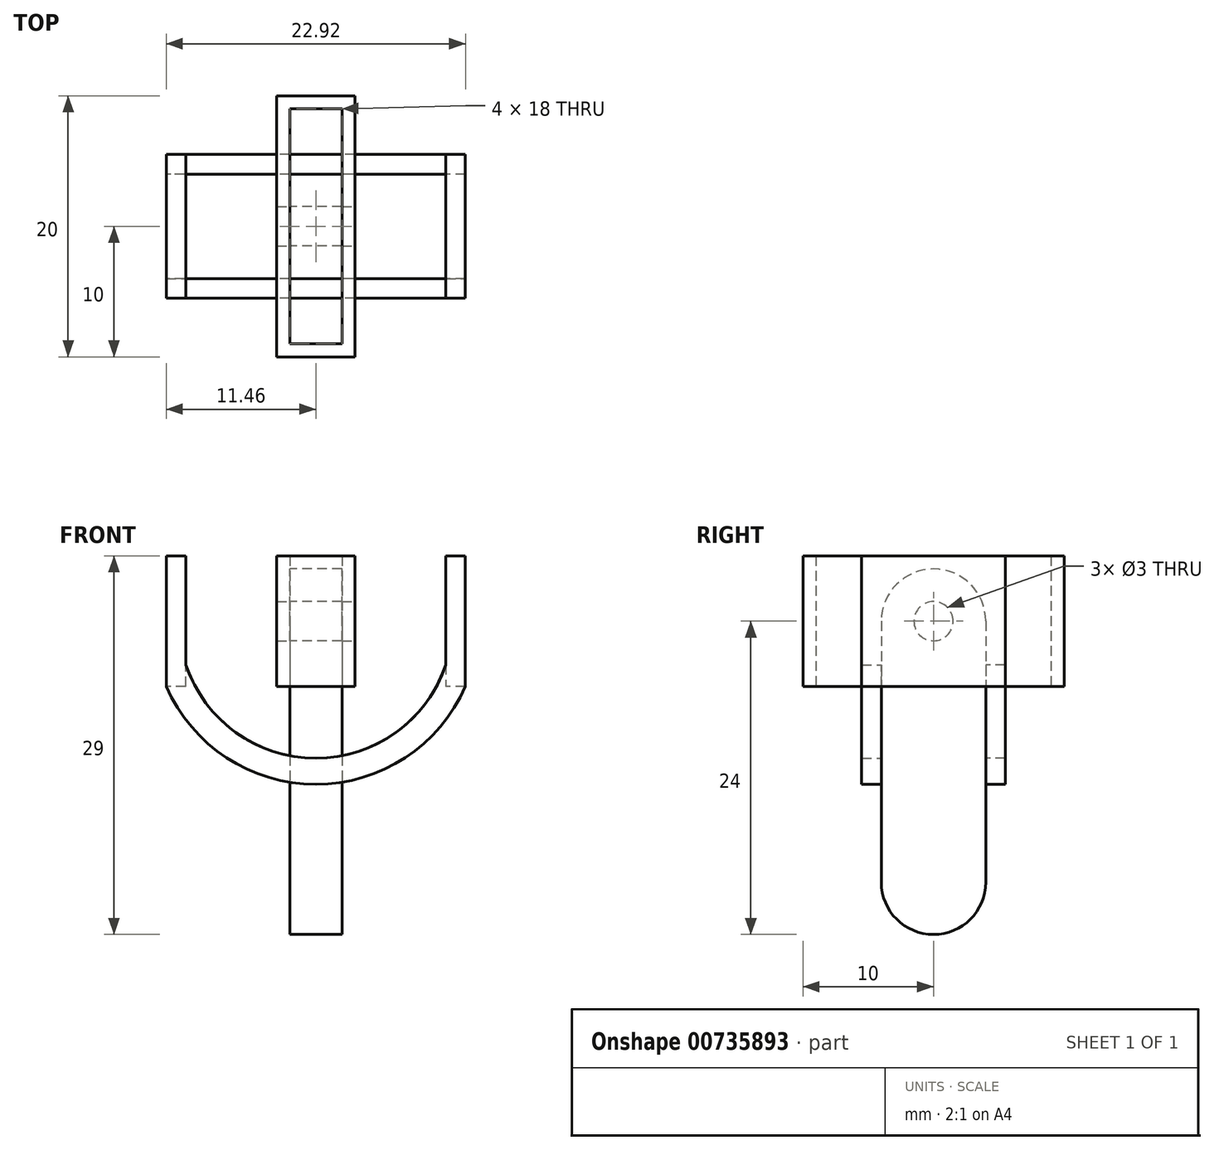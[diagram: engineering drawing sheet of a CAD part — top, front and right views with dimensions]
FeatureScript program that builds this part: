
annotation { "Feature Type Name" : "Feature", "Feature Type Description" : "" }
export const myFeature = defineFeature(function(context is Context, id is Id, definition is map)
    precondition{}
    {
        {
            var Q0;
            Q0=qCreatedBy(makeId("Right.planeOp"),FACE);
            var sketch = newSketch(context, id + "F0", { "sketchPlane" : qUnion([Q0])});
            skCircle(sketch, "E0", {"center": v(0, 0) * mm, "radius": 1.5 * mm});
            skCircle(sketch, "E1", {"center": v(0, 0) * mm, "radius": 4 * mm});
            skCircle(sketch, "E2", {"center": v(0, -20) * mm, "radius": 4 * mm});
            skLineSegment(sketch, "E3", {"start": v(-4, 0) * mm, "end": v(-4, -20) * mm});
            skLineSegment(sketch, "E4", {"start": v(4, 0) * mm, "end": v(4, -20) * mm});
            skSolve(sketch);
        }
        {
            var Q0;
            Q0=makeQuery(id+"F0.imprint","IMPRINT",FACE,{"disambiguationData":[TD([[makeQuery(id+"F0.imprint","IMPRINT",EDGE,{"derivedFrom":sQuery(id+"F0.wireOp",EDGE,"E0")}),-1.0]])]});
            var Q1;
            {var subQ0=sQuery(id+"F0.wireOp",EDGE,"E3");Q1=makeQuery(id+"F0.imprint","IMPRINT",FACE,{"disambiguationData":[TD([[makeQuery(id+"F0.imprint","IMPRINT",EDGE,{"derivedFrom":subQ0}),1.0]])]});}
            var Q2;
            {var subQ0=sQuery(id+"F0.wireOp",EDGE,"E2");var subQ1=makeQuery(id+"F0.imprint","INTERSECT",VERTEX,{"derivedFrom":[subQ0,sQuery(id+"F0.wireOp",EDGE,"E3")]});Q2=makeQuery(id+"F0.imprint","IMPRINT",FACE,{"disambiguationData":[TD([[makeQuery(id+"F0.imprint","IMPRINT",EDGE,{"disambiguationData":[TD([[subQ1,1.0]])],"derivedFrom":subQ0}),1.0]])]});}
            extrude(context, id + "F1", {"entities" : qUnion([Q0, Q1, Q2]), "endBound" : BoundingType.SYMMETRIC, "depth" : 4 * mm, "offsetDistance" : 25 * mm});
        }
        {
            var Q0;
            Q0=qCreatedBy(makeId("Top.planeOp"),FACE);
            var sketch = newSketch(context, id + "F2", { "sketchPlane" : qUnion([Q0])});
            skLineSegment(sketch, "E5.bottom", {"start": v(-2, 9) * mm, "end": v(2, 9) * mm});
            skLineSegment(sketch, "E5.top", {"start": v(-2, -9) * mm, "end": v(2, -9) * mm});
            skLineSegment(sketch, "E5.left", {"start": v(-2, 9) * mm, "end": v(-2, -9) * mm});
            skLineSegment(sketch, "E5.right", {"start": v(2, 9) * mm, "end": v(2, -9) * mm});
            skLineSegment(sketch, "E6.bottom", {"start": v(-3, 10) * mm, "end": v(3, 10) * mm});
            skLineSegment(sketch, "E6.top", {"start": v(-3, -10) * mm, "end": v(3, -10) * mm});
            skLineSegment(sketch, "E6.left", {"start": v(-3, 10) * mm, "end": v(-3, -10) * mm});
            skLineSegment(sketch, "E6.right", {"start": v(3, 10) * mm, "end": v(3, -10) * mm});
            skSolve(sketch);
        }
        {
            var Q0;
            Q0=makeQuery(id+"F2.imprint","IMPRINT",FACE,{"disambiguationData":[TD([[makeQuery(id+"F2.imprint","IMPRINT",EDGE,{"derivedFrom":sQuery(id+"F2.wireOp",EDGE,"E5.bottom")}),1.0]])]});
            extrude(context, id + "F3", {"entities" : qUnion([Q0]), "endBound" : BoundingType.SYMMETRIC, "depth" : 10 * mm, "offsetDistance" : 25 * mm});
        }
        {
            var Q0;
            Q0=makeQuery(id+"F0.imprint","IMPRINT",FACE,{"disambiguationData":[TD([[makeQuery(id+"F0.imprint","IMPRINT",EDGE,{"derivedFrom":sQuery(id+"F0.wireOp",EDGE,"E0")}),1.0]])]});
            extrude(context, id + "F4", {"entities" : qUnion([Q0]), "operationType" : NewBodyOperationType.REMOVE, "endBound" : BoundingType.SYMMETRIC, "oppositeDirection" : true, "depth" : 25 * mm, "offsetDistance" : 25 * mm});
        }
        {
            var Q0;
            Q0=makeQuery(id+"F1.opExtrude","SWEPT_FACE",FACE,{"disambiguationData":[OSD([sQuery(id+"F0.wireOp",EDGE,"E4")])]});
            var sketch = newSketch(context, id + "F5", { "sketchPlane" : qUnion([Q0])});
            skCircle(sketch, "E7", {"center": v(0, 0) * mm, "radius": 10.5 * mm});
            skCircle(sketch, "E8", {"center": v(0, 0) * mm, "radius": 12.5 * mm});
            skLineSegment(sketch, "E9", {"start": v(-11.46, 5) * mm, "end": v(11.46, 5) * mm});
            skLineSegment(sketch, "E10", {"start": v(-11.46, -5) * mm, "end": v(11.46, -5) * mm});
            skLineSegment(sketch, "E11", {"start": v(-11.46, 5) * mm, "end": v(-11.46, -5) * mm});
            skLineSegment(sketch, "E12", {"start": v(11.46, 5) * mm, "end": v(11.46, -5) * mm});
            skLineSegment(sketch, "E13", {"start": v(9.96, 5) * mm, "end": v(9.96, -5) * mm});
            skLineSegment(sketch, "E14", {"start": v(-9.96, 5) * mm, "end": v(-9.96, -5) * mm});
            skSolve(sketch);
        }
        {
            var Q0;
            {var subQ6=sQuery(id+"F5.wireOp",EDGE,"E11");Q0=makeQuery(id+"F5.imprint","IMPRINT",FACE,{"disambiguationData":[TD([[makeQuery(id+"F5.imprint","IMPRINT",EDGE,{"derivedFrom":subQ6}),1.0]])]});}
            var Q1;
            {var subQ0=sQuery(id+"F5.wireOp",EDGE,"lFEVrdAN-HZwF-8sQD-rMAo-F9QIEANWM2wr");Q1=makeQuery(id+"F5.imprint","IMPRINT",FACE,{"disambiguationData":[TD([[makeQuery(id+"F5.imprint","IMPRINT",EDGE,{"derivedFrom":subQ0}),-1.0]])]});}
            var Q2;
            {var subQ3=sQuery(id+"F5.wireOp",EDGE,"E7");var subQ7=makeQuery(id+"F5.imprint","INTERSECT",VERTEX,{"disambiguationData":[OD(0.0)],"derivedFrom":[subQ3,sQuery(id+"F5.wireOp",EDGE,"iSYoZpPV-LOci-Hl4O-fSi4-jdDNIl23jevi")]});Q2=makeQuery(id+"F5.imprint","IMPRINT",FACE,{"disambiguationData":[TD([[makeQuery(id+"F5.imprint","IMPRINT",EDGE,{"disambiguationData":[TD([[subQ7,-1.0]])],"derivedFrom":subQ3}),-1.0]])]});}
            var Q3;
            {var subQ0=sQuery(id+"F5.wireOp",EDGE,"E7");var subQ1=sQuery(id+"F0.wireOp",EDGE,"E4");var subQ2=makeQuery(id+"F1.opExtrude","CAP_EDGE",EDGE,{"disambiguationData":[OSD([subQ1])],"isStart":false});var subQ3=makeQuery(id+"F5.imprint","INTERSECT",VERTEX,{"derivedFrom":[subQ2,subQ0]});Q3=makeQuery(id+"F5.imprint","IMPRINT",FACE,{"disambiguationData":[TD([[makeQuery(id+"F5.imprint","IMPRINT",EDGE,{"disambiguationData":[TD([[subQ3,-1.0]])],"derivedFrom":subQ0}),-1.0]])]});}
            var Q4;
            {var subQ3=sQuery(id+"F5.wireOp",EDGE,"E7");var subQ7=makeQuery(id+"F5.imprint","INTERSECT",VERTEX,{"disambiguationData":[OD(1.0)],"derivedFrom":[subQ3,sQuery(id+"F5.wireOp",EDGE,"iSYoZpPV-LOci-Hl4O-fSi4-jdDNIl23jevi")]});Q4=makeQuery(id+"F5.imprint","IMPRINT",FACE,{"disambiguationData":[TD([[makeQuery(id+"F5.imprint","IMPRINT",EDGE,{"disambiguationData":[TD([[subQ7,1.0]])],"derivedFrom":subQ3}),-1.0]])]});}
            var Q5;
            {var subQ6=sQuery(id+"F5.wireOp",EDGE,"E12");Q5=makeQuery(id+"F5.imprint","IMPRINT",FACE,{"disambiguationData":[TD([[makeQuery(id+"F5.imprint","IMPRINT",EDGE,{"derivedFrom":subQ6}),-1.0]])]});}
            var Q6;
            {var subQ0=sQuery(id+"F5.wireOp",EDGE,"WG5NRfXU-aEiA-IK5w-2DdL-H3FO2lLHFPoR");Q6=makeQuery(id+"F5.imprint","IMPRINT",FACE,{"disambiguationData":[TD([[makeQuery(id+"F5.imprint","IMPRINT",EDGE,{"derivedFrom":subQ0}),1.0]])]});}
            var Q7;
            {var subQ0=sQuery(id+"F5.wireOp",EDGE,"E13");var subQ1=sQuery(id+"F5.wireOp",EDGE,"E7");var subQ2=makeQuery(id+"F5.imprint","INTERSECT",VERTEX,{"disambiguationData":[OD(0.0)],"derivedFrom":[subQ1,subQ0]});Q7=makeQuery(id+"F5.imprint","IMPRINT",FACE,{"disambiguationData":[TD([[makeQuery(id+"F5.imprint","IMPRINT",EDGE,{"disambiguationData":[TD([[subQ2,1.0]])],"derivedFrom":subQ1}),1.0]])]});}
            var Q8;
            {var subQ0=sQuery(id+"F5.wireOp",EDGE,"E10");var subQ2=sQuery(id+"F5.wireOp",EDGE,"E7");var subQ3=makeQuery(id+"F5.imprint","INTERSECT",VERTEX,{"disambiguationData":[OD(1.0)],"derivedFrom":[subQ2,subQ0]});Q8=makeQuery(id+"F5.imprint","IMPRINT",FACE,{"disambiguationData":[TD([[makeQuery(id+"F5.imprint","IMPRINT",EDGE,{"disambiguationData":[TD([[subQ3,1.0]])],"derivedFrom":subQ2}),-1.0]])]});}
            var Q9;
            {var subQ0=sQuery(id+"F5.wireOp",EDGE,"E10");var subQ4=sQuery(id+"F5.wireOp",EDGE,"E7");var subQ5=makeQuery(id+"F5.imprint","INTERSECT",VERTEX,{"disambiguationData":[OD(0.0)],"derivedFrom":[subQ4,subQ0]});Q9=makeQuery(id+"F5.imprint","IMPRINT",FACE,{"disambiguationData":[TD([[makeQuery(id+"F5.imprint","IMPRINT",EDGE,{"disambiguationData":[TD([[subQ5,-1.0]])],"derivedFrom":subQ4}),-1.0]])]});}
            var Q10;
            {var subQ0=sQuery(id+"F5.wireOp",EDGE,"E14");var subQ1=sQuery(id+"F5.wireOp",EDGE,"E7");var subQ2=makeQuery(id+"F5.imprint","INTERSECT",VERTEX,{"disambiguationData":[OD(1.0)],"derivedFrom":[subQ1,subQ0]});Q10=makeQuery(id+"F5.imprint","IMPRINT",FACE,{"disambiguationData":[TD([[makeQuery(id+"F5.imprint","IMPRINT",EDGE,{"disambiguationData":[TD([[subQ2,-1.0]])],"derivedFrom":subQ1}),-1.0]])]});}
            var Q11;
            {var subQ0=sQuery(id+"F5.wireOp",EDGE,"E14");var subQ1=sQuery(id+"F5.wireOp",EDGE,"E7");var subQ2=makeQuery(id+"F5.imprint","INTERSECT",VERTEX,{"disambiguationData":[OD(0.0)],"derivedFrom":[subQ1,subQ0]});Q11=makeQuery(id+"F5.imprint","IMPRINT",FACE,{"disambiguationData":[TD([[makeQuery(id+"F5.imprint","IMPRINT",EDGE,{"disambiguationData":[TD([[subQ2,-1.0]])],"derivedFrom":subQ1}),1.0]])]});}
            var Q12;
            {var subQ0=sQuery(id+"F5.wireOp",EDGE,"E10");var subQ1=sQuery(id+"F5.wireOp",EDGE,"E7");var subQ2=makeQuery(id+"F5.imprint","INTERSECT",VERTEX,{"disambiguationData":[OD(1.0)],"derivedFrom":[subQ1,subQ0]});Q12=makeQuery(id+"F5.imprint","IMPRINT",FACE,{"disambiguationData":[TD([[makeQuery(id+"F5.imprint","IMPRINT",EDGE,{"disambiguationData":[TD([[subQ2,-1.0]])],"derivedFrom":subQ1}),-1.0]])]});}
            extrude(context, id + "F6", {"entities" : qUnion([Q0, Q1, Q2, Q3, Q4, Q5, Q6, Q7, Q8, Q9, Q10, Q11, Q12]), "depth" : 1.5 * mm, "offsetDistance" : 25 * mm});
        }
        {
            var Q0;
            {var subQ6=sQuery(id+"F5.wireOp",EDGE,"E12");Q0=makeQuery(id+"F5.imprint","IMPRINT",FACE,{"disambiguationData":[TD([[makeQuery(id+"F5.imprint","IMPRINT",EDGE,{"derivedFrom":subQ6}),-1.0]])]});}
            var Q1;
            {var subQ0=sQuery(id+"F5.wireOp",EDGE,"WG5NRfXU-aEiA-IK5w-2DdL-H3FO2lLHFPoR");Q1=makeQuery(id+"F5.imprint","IMPRINT",FACE,{"disambiguationData":[TD([[makeQuery(id+"F5.imprint","IMPRINT",EDGE,{"derivedFrom":subQ0}),1.0]])]});}
            var Q2;
            {var subQ0=sQuery(id+"F5.wireOp",EDGE,"lFEVrdAN-HZwF-8sQD-rMAo-F9QIEANWM2wr");Q2=makeQuery(id+"F5.imprint","IMPRINT",FACE,{"disambiguationData":[TD([[makeQuery(id+"F5.imprint","IMPRINT",EDGE,{"derivedFrom":subQ0}),-1.0]])]});}
            var Q3;
            {var subQ6=sQuery(id+"F5.wireOp",EDGE,"E11");Q3=makeQuery(id+"F5.imprint","IMPRINT",FACE,{"disambiguationData":[TD([[makeQuery(id+"F5.imprint","IMPRINT",EDGE,{"derivedFrom":subQ6}),1.0]])]});}
            var Q4;
            {var subQ0=sQuery(id+"F5.wireOp",EDGE,"E13");var subQ1=sQuery(id+"F5.wireOp",EDGE,"E7");var subQ2=makeQuery(id+"F5.imprint","INTERSECT",VERTEX,{"disambiguationData":[OD(0.0)],"derivedFrom":[subQ1,subQ0]});Q4=makeQuery(id+"F5.imprint","IMPRINT",FACE,{"disambiguationData":[TD([[makeQuery(id+"F5.imprint","IMPRINT",EDGE,{"disambiguationData":[TD([[subQ2,1.0]])],"derivedFrom":subQ1}),1.0]])]});}
            var Q5;
            {var subQ0=sQuery(id+"F5.wireOp",EDGE,"E14");var subQ1=sQuery(id+"F5.wireOp",EDGE,"E7");var subQ2=makeQuery(id+"F5.imprint","INTERSECT",VERTEX,{"disambiguationData":[OD(0.0)],"derivedFrom":[subQ1,subQ0]});Q5=makeQuery(id+"F5.imprint","IMPRINT",FACE,{"disambiguationData":[TD([[makeQuery(id+"F5.imprint","IMPRINT",EDGE,{"disambiguationData":[TD([[subQ2,-1.0]])],"derivedFrom":subQ1}),1.0]])]});}
            var Q6;
            Q6=makeQuery(id+"F1.opExtrude","SWEPT_FACE",FACE,{"disambiguationData":[OSD([sQuery(id+"F0.wireOp",EDGE,"E3")])]});
            extrude(context, id + "F7", {"entities" : qUnion([Q0, Q1, Q2, Q3, Q4, Q5]), "operationType" : NewBodyOperationType.ADD, "endBound" : BoundingType.UP_TO_SURFACE, "oppositeDirection" : true, "depth" : 25 * mm, "endBoundEntityFace" : qUnion([Q6]), "offsetDistance" : 25 * mm});
        }
        {
            var Q0;
            {var subQ6=sQuery(id+"F5.wireOp",EDGE,"E11");Q0=makeQuery(id+"F5.imprint","IMPRINT",FACE,{"disambiguationData":[TD([[makeQuery(id+"F5.imprint","IMPRINT",EDGE,{"derivedFrom":subQ6}),1.0]])]});}
            var Q1;
            {var subQ0=sQuery(id+"F5.wireOp",EDGE,"lFEVrdAN-HZwF-8sQD-rMAo-F9QIEANWM2wr");Q1=makeQuery(id+"F5.imprint","IMPRINT",FACE,{"disambiguationData":[TD([[makeQuery(id+"F5.imprint","IMPRINT",EDGE,{"derivedFrom":subQ0}),-1.0]])]});}
            var Q2;
            {var subQ0=sQuery(id+"F5.wireOp",EDGE,"WG5NRfXU-aEiA-IK5w-2DdL-H3FO2lLHFPoR");Q2=makeQuery(id+"F5.imprint","IMPRINT",FACE,{"disambiguationData":[TD([[makeQuery(id+"F5.imprint","IMPRINT",EDGE,{"derivedFrom":subQ0}),1.0]])]});}
            var Q3;
            {var subQ6=sQuery(id+"F5.wireOp",EDGE,"E12");Q3=makeQuery(id+"F5.imprint","IMPRINT",FACE,{"disambiguationData":[TD([[makeQuery(id+"F5.imprint","IMPRINT",EDGE,{"derivedFrom":subQ6}),-1.0]])]});}
            var Q4;
            {var subQ3=makeQuery(id+"F1.opExtrude","CAP_EDGE",EDGE,{"disambiguationData":[OSD([sQuery(id+"F0.wireOp",EDGE,"E4")])],"isStart":true});var subQ5=sQuery(id+"F5.wireOp",EDGE,"E8");var subQ7=makeQuery(id+"F5.imprint","INTERSECT",VERTEX,{"derivedFrom":[subQ3,subQ5]});Q4=makeQuery(id+"F5.imprint","IMPRINT",FACE,{"disambiguationData":[TD([[makeQuery(id+"F5.imprint","IMPRINT",EDGE,{"disambiguationData":[TD([[subQ7,1.0]])],"derivedFrom":subQ3}),1.0]])]});}
            var Q5;
            {var subQ3=makeQuery(id+"F1.opExtrude","CAP_EDGE",EDGE,{"disambiguationData":[OSD([sQuery(id+"F0.wireOp",EDGE,"E4")])],"isStart":false});var subQ5=sQuery(id+"F5.wireOp",EDGE,"E8");var subQ6=makeQuery(id+"F5.imprint","INTERSECT",VERTEX,{"derivedFrom":[subQ3,subQ5]});Q5=makeQuery(id+"F5.imprint","IMPRINT",FACE,{"disambiguationData":[TD([[makeQuery(id+"F5.imprint","IMPRINT",EDGE,{"disambiguationData":[TD([[subQ6,1.0]])],"derivedFrom":subQ3}),-1.0]])]});}
            var Q6;
            {var subQ0=sQuery(id+"F5.wireOp",EDGE,"E7");var subQ1=sQuery(id+"F0.wireOp",EDGE,"E4");var subQ2=makeQuery(id+"F1.opExtrude","CAP_EDGE",EDGE,{"disambiguationData":[OSD([subQ1])],"isStart":false});var subQ3=makeQuery(id+"F5.imprint","INTERSECT",VERTEX,{"derivedFrom":[subQ2,subQ0]});Q6=makeQuery(id+"F5.imprint","IMPRINT",FACE,{"disambiguationData":[TD([[makeQuery(id+"F5.imprint","IMPRINT",EDGE,{"disambiguationData":[TD([[subQ3,-1.0]])],"derivedFrom":subQ0}),-1.0]])]});}
            var Q7;
            {var subQ0=sQuery(id+"F5.wireOp",EDGE,"E13");var subQ1=sQuery(id+"F5.wireOp",EDGE,"E7");var subQ2=makeQuery(id+"F5.imprint","INTERSECT",VERTEX,{"disambiguationData":[OD(0.0)],"derivedFrom":[subQ1,subQ0]});Q7=makeQuery(id+"F5.imprint","IMPRINT",FACE,{"disambiguationData":[TD([[makeQuery(id+"F5.imprint","IMPRINT",EDGE,{"disambiguationData":[TD([[subQ2,1.0]])],"derivedFrom":subQ1}),1.0]])]});}
            var Q8;
            {var subQ0=sQuery(id+"F5.wireOp",EDGE,"E14");var subQ1=sQuery(id+"F5.wireOp",EDGE,"E7");var subQ2=makeQuery(id+"F5.imprint","INTERSECT",VERTEX,{"disambiguationData":[OD(0.0)],"derivedFrom":[subQ1,subQ0]});Q8=makeQuery(id+"F5.imprint","IMPRINT",FACE,{"disambiguationData":[TD([[makeQuery(id+"F5.imprint","IMPRINT",EDGE,{"disambiguationData":[TD([[subQ2,-1.0]])],"derivedFrom":subQ1}),1.0]])]});}
            var Q9;
            {var subQ0=sQuery(id+"F5.wireOp",EDGE,"E10");var subQ1=sQuery(id+"F5.wireOp",EDGE,"E7");var subQ2=makeQuery(id+"F5.imprint","INTERSECT",VERTEX,{"disambiguationData":[OD(1.0)],"derivedFrom":[subQ1,subQ0]});Q9=makeQuery(id+"F5.imprint","IMPRINT",FACE,{"disambiguationData":[TD([[makeQuery(id+"F5.imprint","IMPRINT",EDGE,{"disambiguationData":[TD([[subQ2,-1.0]])],"derivedFrom":subQ1}),-1.0]])]});}
            var Q10;
            {var subQ0=sQuery(id+"F5.wireOp",EDGE,"E14");var subQ1=sQuery(id+"F5.wireOp",EDGE,"E7");var subQ2=makeQuery(id+"F5.imprint","INTERSECT",VERTEX,{"disambiguationData":[OD(1.0)],"derivedFrom":[subQ1,subQ0]});Q10=makeQuery(id+"F5.imprint","IMPRINT",FACE,{"disambiguationData":[TD([[makeQuery(id+"F5.imprint","IMPRINT",EDGE,{"disambiguationData":[TD([[subQ2,-1.0]])],"derivedFrom":subQ1}),-1.0]])]});}
            extrude(context, id + "F8", {"entities" : qUnion([Q0, Q1, Q2, Q3, Q4, Q5, Q6, Q7, Q8, Q9, Q10]), "operationType" : NewBodyOperationType.ADD, "oppositeDirection" : true, "depth" : 9.5 * mm, "offsetDistance" : 25 * mm, "hasSecondDirection" : true, "secondDirectionOppositeDirection" : true, "secondDirectionDepth" : 8 * mm});
        }
    });
